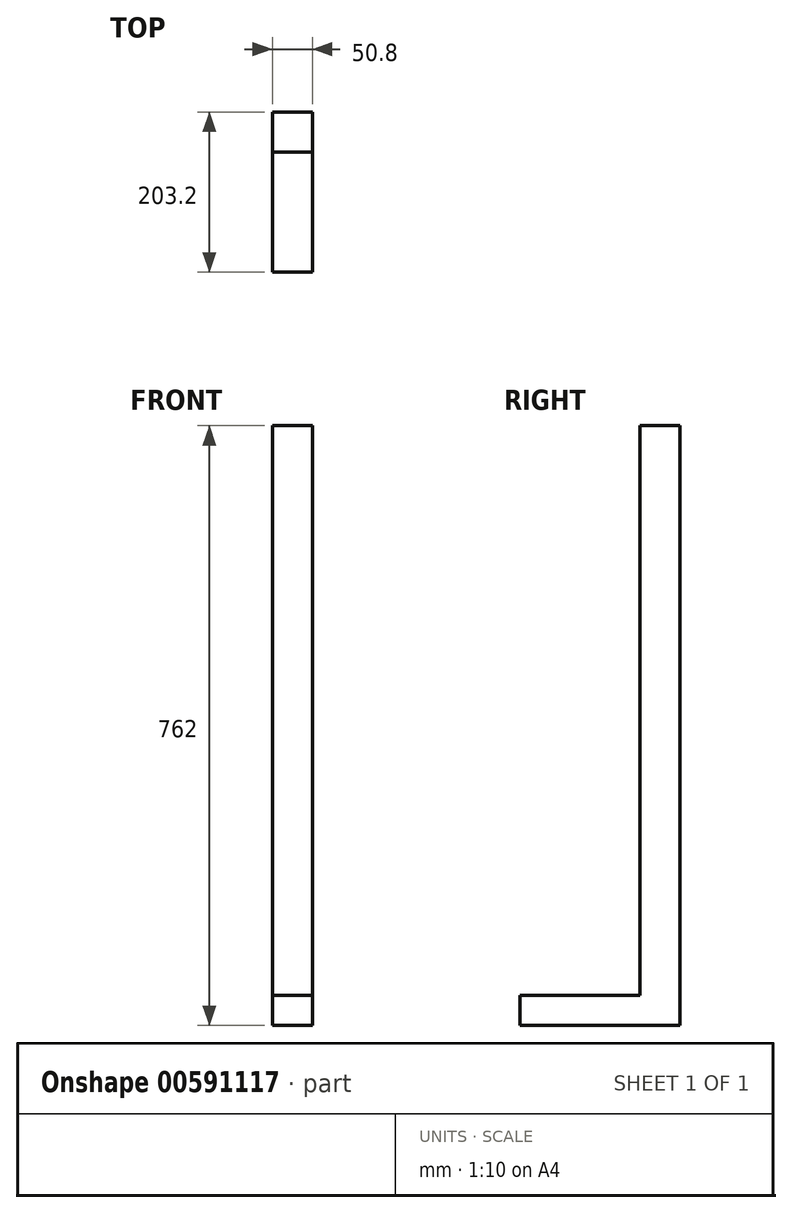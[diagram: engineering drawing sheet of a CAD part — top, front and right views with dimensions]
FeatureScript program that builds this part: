
annotation { "Feature Type Name" : "Feature", "Feature Type Description" : "" }
export const myFeature = defineFeature(function(context is Context, id is Id, definition is map)
    precondition{}
    {
        {
            var Q0;
            Q0=qCreatedBy(makeId("Top.planeOp"),FACE);
            var sketch = newSketch(context, id + "F0", { "sketchPlane" : qUnion([Q0])});
            skLineSegment(sketch, "E0.bottom", {"start": v(-27.87, 25.9) * mm, "end": v(22.93, 25.9) * mm});
            skLineSegment(sketch, "E0.top", {"start": v(-27.87, -24.9) * mm, "end": v(22.93, -24.9) * mm});
            skLineSegment(sketch, "E0.left", {"start": v(-27.87, 25.9) * mm, "end": v(-27.87, -24.9) * mm});
            skLineSegment(sketch, "E0.right", {"start": v(22.93, 25.9) * mm, "end": v(22.93, -24.9) * mm});
            skSolve(sketch);
        }
        {
            var Q0;
            Q0 = qSketchRegion(id + "F0", true);
            extrude(context, id + "F1", {"entities" : qUnion([Q0]), "depth" : 762 * mm, "offsetDistance" : 25.4 * mm});
        }
        {
            var Q0;
            Q0=makeQuery(id+"F1.opExtrude","SWEPT_FACE",FACE,{"disambiguationData":[OSD([sQuery(id+"F0.wireOp",EDGE,"E0.top")])]});
            var sketch = newSketch(context, id + "F2", { "sketchPlane" : qUnion([Q0])});
            skLineSegment(sketch, "E1.bottom", {"start": v(-27.87, 38.2) * mm, "end": v(200.73, 38.2) * mm});
            skLineSegment(sketch, "E1.top", {"start": v(-27.87, 0) * mm, "end": v(200.73, 0) * mm});
            skLineSegment(sketch, "E1.left", {"start": v(-27.87, 38.2) * mm, "end": v(-27.87, 0) * mm});
            skLineSegment(sketch, "E1.right", {"start": v(200.73, 38.2) * mm, "end": v(200.73, 0) * mm});
            skSolve(sketch);
        }
        {
            var Q0;
            {var subQ0=sQuery(id+"F2.wireOp",EDGE,"E1.left");Q0=makeQuery(id+"F2.imprint","IMPRINT",FACE,{"disambiguationData":[TD([[makeQuery(id+"F2.imprint","IMPRINT",EDGE,{"derivedFrom":subQ0}),1.0]])]});}
            extrude(context, id + "F3", {"entities" : qUnion([Q0]), "operationType" : NewBodyOperationType.ADD, "depth" : 152.4 * mm, "offsetDistance" : 25.4 * mm});
        }
    });
